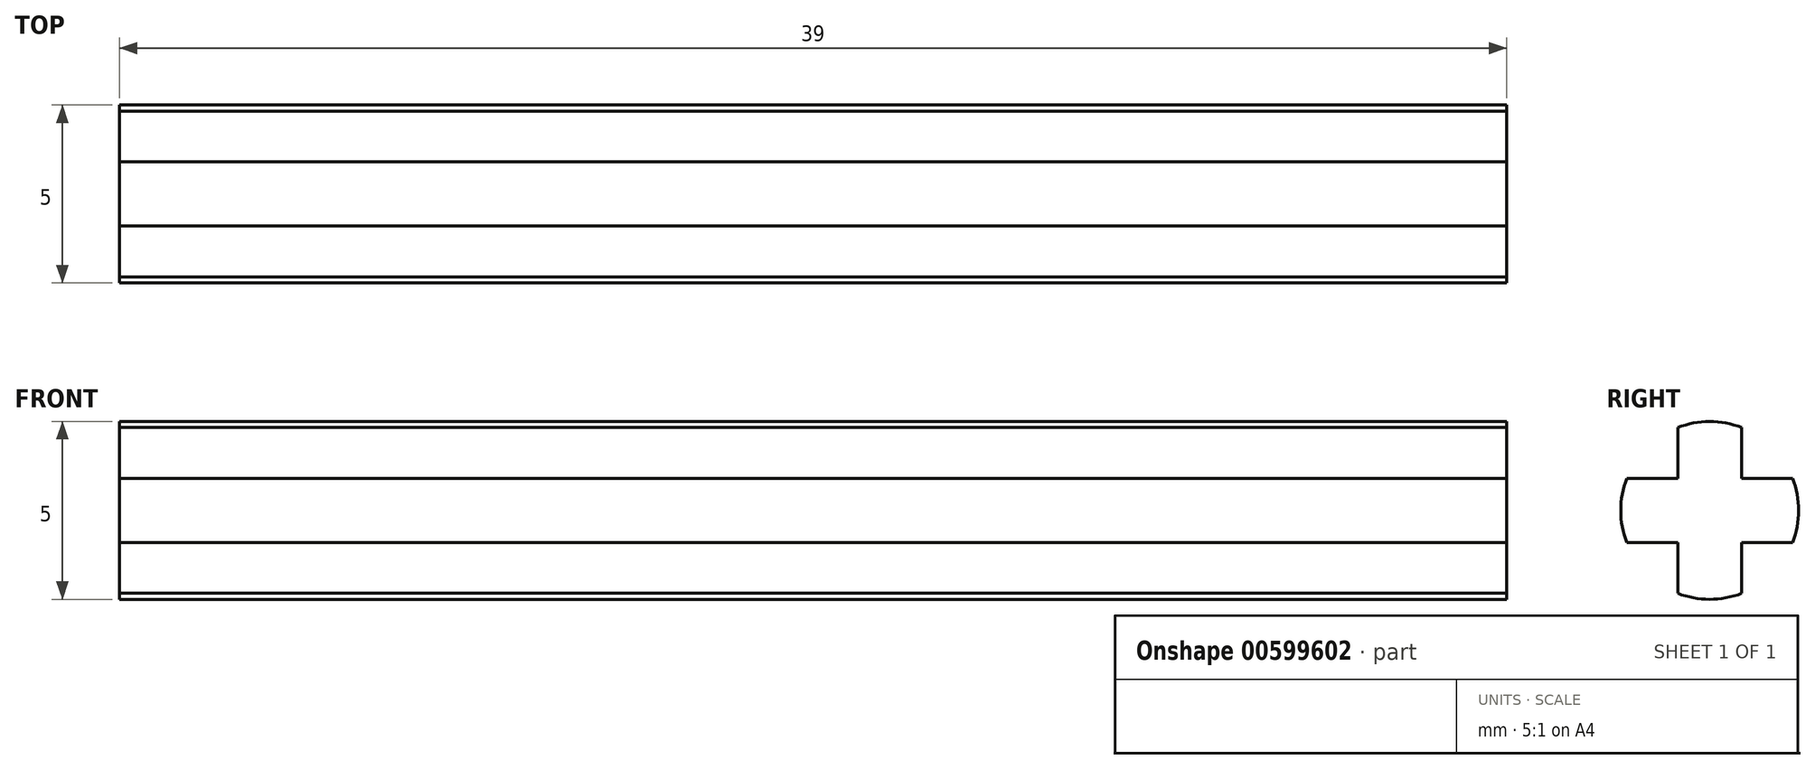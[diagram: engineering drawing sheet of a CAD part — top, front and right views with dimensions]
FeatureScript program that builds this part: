
annotation { "Feature Type Name" : "Feature", "Feature Type Description" : "" }
export const myFeature = defineFeature(function(context is Context, id is Id, definition is map)
    precondition{}
    {
        {
            var Q0;
            Q0=qCreatedBy(makeId("Right.planeOp"),FACE);
            var sketch = newSketch(context, id + "F0", { "sketchPlane" : qUnion([Q0])});
            skArc(sketch, "E0", {"start": v(2.33, -0.9) * mm, "mid": v(2.5, 0) * mm, "end": v(2.33, 0.9) * mm});
            skLineSegment(sketch, "E1.left", {"start": v(-0.9, 2.33) * mm, "end": v(-0.9, 0.9) * mm});
            skLineSegment(sketch, "E1.right", {"start": v(0.9, 2.33) * mm, "end": v(0.9, 0.9) * mm});
            skLineSegment(sketch, "E2.bottom", {"start": v(2.33, 0.9) * mm, "end": v(0.9, 0.9) * mm});
            skLineSegment(sketch, "E2.top", {"start": v(2.33, -0.9) * mm, "end": v(0.9, -0.9) * mm});
            skArc(sketch, "E3.trimOffspring", {"start": v(0.9, 2.33) * mm, "mid": v(0, 2.5) * mm, "end": v(-0.9, 2.33) * mm});
            skArc(sketch, "E4.trimOffspring", {"start": v(-2.33, 0.9) * mm, "mid": v(-2.5, 0) * mm, "end": v(-2.33, -0.9) * mm});
            skArc(sketch, "E5.trimOffspring", {"start": v(-0.9, -2.33) * mm, "mid": v(0, -2.5) * mm, "end": v(0.9, -2.33) * mm});
            skLineSegment(sketch, "E6.trimOffspring", {"start": v(-0.9, -0.9) * mm, "end": v(-0.9, -2.33) * mm});
            skLineSegment(sketch, "E7.trimOffspring", {"start": v(-0.9, 0.9) * mm, "end": v(-2.33, 0.9) * mm});
            skLineSegment(sketch, "E8.trimOffspring", {"start": v(0.9, -0.9) * mm, "end": v(0.9, -2.33) * mm});
            skLineSegment(sketch, "E9.trimOffspring", {"start": v(-0.9, -0.9) * mm, "end": v(-2.33, -0.9) * mm});
            skSolve(sketch);
        }
        {
            var Q0;
            Q0 = qSketchRegion(id + "F0", true);
            extrude(context, id + "F1", {"entities" : qUnion([Q0]), "depth" : 39 * mm, "offsetDistance" : 25 * mm});
        }
    });
